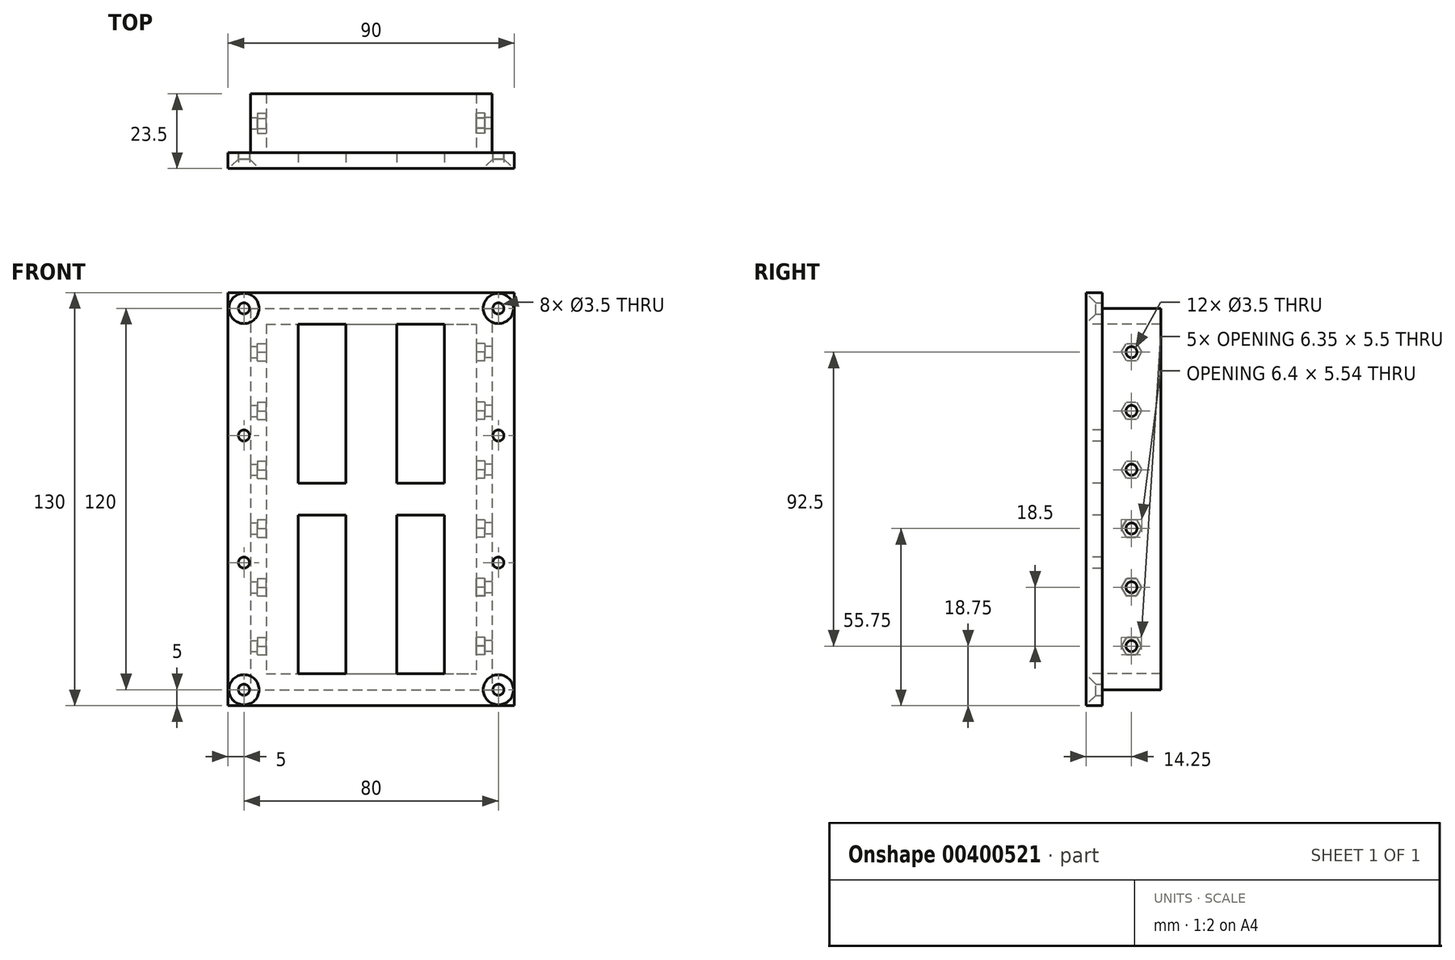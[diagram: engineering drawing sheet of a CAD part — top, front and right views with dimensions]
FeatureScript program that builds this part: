
annotation { "Feature Type Name" : "Feature", "Feature Type Description" : "" }
export const myFeature = defineFeature(function(context is Context, id is Id, definition is map)
    precondition{}
    {
        {
            var Q0;
            Q0=qCreatedBy(makeId("Front.planeOp"),FACE);
            var sketch = newSketch(context, id + "F0", { "sketchPlane" : qUnion([Q0])});
            skLineSegment(sketch, "E0.bottom", {"start": v(-33, 55) * mm, "end": v(33, 55) * mm});
            skLineSegment(sketch, "E0.top", {"start": v(-33, -55) * mm, "end": v(33, -55) * mm});
            skLineSegment(sketch, "E0.left", {"start": v(-33, 55) * mm, "end": v(-33, -55) * mm});
            skLineSegment(sketch, "E0.right", {"start": v(33, 55) * mm, "end": v(33, -55) * mm});
            skPoint(sketch, "E0.middle", {"position": v(0, 0) * mm});
            skLineSegment(sketch, "E1.bottom", {"start": v(-38, 60) * mm, "end": v(38, 60) * mm});
            skLineSegment(sketch, "E1.top", {"start": v(-38, -60) * mm, "end": v(38, -60) * mm});
            skLineSegment(sketch, "E1.left", {"start": v(-38, 60) * mm, "end": v(-38, -60) * mm});
            skLineSegment(sketch, "E1.right", {"start": v(38, 60) * mm, "end": v(38, -60) * mm});
            skSolve(sketch);
        }
        {
            var Q0;
            Q0 = qSketchRegion(id + "F0", true);
            extrude(context, id + "F1", {"entities" : qUnion([Q0]), "oppositeDirection" : true, "depth" : 18.5 * mm});
        }
        {
            var Q0;
            Q0=makeQuery(id+"F1.opExtrude","CAP_FACE",FACE,{"disambiguationData":[OSD([sQuery(id+"F0.wireOp",EDGE,"E0.bottom"),sQuery(id+"F0.wireOp",EDGE,"E0.top"),sQuery(id+"F0.wireOp",EDGE,"E0.left"),sQuery(id+"F0.wireOp",EDGE,"E0.right"),sQuery(id+"F0.wireOp",EDGE,"E1.bottom"),sQuery(id+"F0.wireOp",EDGE,"E1.top"),sQuery(id+"F0.wireOp",EDGE,"E1.left"),sQuery(id+"F0.wireOp",EDGE,"E1.right")])],"isStart":true});
            var sketch = newSketch(context, id + "F2", { "sketchPlane" : qUnion([Q0])});
            skLineSegment(sketch, "E2.bottom", {"start": v(-45, 65) * mm, "end": v(45, 65) * mm});
            skLineSegment(sketch, "E2.top", {"start": v(-45, -65) * mm, "end": v(45, -65) * mm});
            skLineSegment(sketch, "E2.left", {"start": v(-45, 65) * mm, "end": v(-45, -65) * mm});
            skLineSegment(sketch, "E2.right", {"start": v(45, 65) * mm, "end": v(45, -65) * mm});
            skPoint(sketch, "E2.middle", {"position": v(0, 0) * mm});
            skCircle(sketch, "E3", {"center": v(-40, 60) * mm, "radius": 1.75 * mm});
            skCircle(sketch, "E4", {"center": v(40, 60) * mm, "radius": 1.75 * mm});
            skCircle(sketch, "E5", {"center": v(40, -60) * mm, "radius": 1.75 * mm});
            skCircle(sketch, "E6", {"center": v(-40, -60) * mm, "radius": 1.75 * mm});
            skSolve(sketch);
        }
        {
            var Q0;
            Q0=makeQuery(id+"F2.imprint","IMPRINT",FACE,{"disambiguationData":[TD([[makeQuery(id+"F2.imprint","IMPRINT",EDGE,{"derivedFrom":sQuery(id+"F2.wireOp",EDGE,"E2.bottom")}),-1.0]])]});
            var Q1;
            Q1=makeQuery(id+"F2.imprint","IMPRINT",FACE,{"disambiguationData":[TD([[makeQuery(id+"F2.imprint","IMPRINT",EDGE,{"derivedFrom":makeQuery(id+"F1.opExtrude","CAP_EDGE",EDGE,{"disambiguationData":[OSD([sQuery(id+"F0.wireOp",EDGE,"E0.bottom")])],"isStart":true})}),1.0]])]});
            extrude(context, id + "F3", {"entities" : qUnion([Q0, Q1]), "operationType" : NewBodyOperationType.ADD, "depth" : 5 * mm});
        }
        {
            var Q0;
            Q0=makeQuery(id+"F3.opExtrude","CAP_FACE",FACE,{"disambiguationData":[OSD([sQuery(id+"F0.wireOp",EDGE,"E0.bottom"),sQuery(id+"F0.wireOp",EDGE,"E0.top"),sQuery(id+"F0.wireOp",EDGE,"E0.left"),sQuery(id+"F0.wireOp",EDGE,"E0.right"),sQuery(id+"F2.wireOp",EDGE,"E2.bottom"),sQuery(id+"F2.wireOp",EDGE,"E2.top"),sQuery(id+"F2.wireOp",EDGE,"E2.left"),sQuery(id+"F2.wireOp",EDGE,"E2.right"),sQuery(id+"F2.wireOp",EDGE,"E3"),sQuery(id+"F2.wireOp",EDGE,"E4"),sQuery(id+"F2.wireOp",EDGE,"E5"),sQuery(id+"F2.wireOp",EDGE,"E6")])],"isStart":false});
            var sketch = newSketch(context, id + "F4", { "sketchPlane" : qUnion([Q0])});
            skLineSegment(sketch, "E7.bottom", {"start": v(-33, 55) * mm, "end": v(-23, 55) * mm});
            skLineSegment(sketch, "E7.top", {"start": v(-33, -55) * mm, "end": v(-23, -55) * mm});
            skLineSegment(sketch, "E7.left", {"start": v(-33, 55) * mm, "end": v(-33, -55) * mm});
            skLineSegment(sketch, "E7.right", {"start": v(-23, 55) * mm, "end": v(-23, 5) * mm});
            skLineSegment(sketch, "E8.bottom", {"start": v(33, 55) * mm, "end": v(23, 55) * mm});
            skLineSegment(sketch, "E8.top", {"start": v(33, -55) * mm, "end": v(23, -55) * mm});
            skLineSegment(sketch, "E8.left", {"start": v(33, 55) * mm, "end": v(33, -55) * mm});
            skLineSegment(sketch, "E8.right", {"start": v(23, 55) * mm, "end": v(23, 5) * mm});
            skLineSegment(sketch, "E9.bottom", {"start": v(-8, 55) * mm, "end": v(8, 55) * mm});
            skLineSegment(sketch, "E9.top", {"start": v(-8, -55) * mm, "end": v(8, -55) * mm});
            skLineSegment(sketch, "E9.left", {"start": v(-8, 55) * mm, "end": v(-8, 5) * mm});
            skLineSegment(sketch, "E9.right", {"start": v(8, 55) * mm, "end": v(8, 5) * mm});
            skLineSegment(sketch, "E10.bottom", {"start": v(-23, 5) * mm, "end": v(-8, 5) * mm});
            skLineSegment(sketch, "E10.top", {"start": v(-23, -5) * mm, "end": v(-8, -5) * mm});
            skLineSegment(sketch, "E10.left", {"start": v(-33, 5) * mm, "end": v(-33, -5) * mm});
            skLineSegment(sketch, "E10.right", {"start": v(33, 5) * mm, "end": v(33, -5) * mm});
            skPoint(sketch, "E10.middle", {"position": v(0, 0) * mm});
            skLineSegment(sketch, "E11.trimOffspring", {"start": v(-23, -5) * mm, "end": v(-23, -55) * mm});
            skLineSegment(sketch, "E12.trimOffspring", {"start": v(-8, -5) * mm, "end": v(-8, -55) * mm});
            skLineSegment(sketch, "E13.trimOffspring", {"start": v(8, 5) * mm, "end": v(23, 5) * mm});
            skLineSegment(sketch, "E14.trimOffspring", {"start": v(8, -5) * mm, "end": v(23, -5) * mm});
            skLineSegment(sketch, "E15.trimOffspring", {"start": v(8, -5) * mm, "end": v(8, -55) * mm});
            skLineSegment(sketch, "E16.trimOffspring", {"start": v(23, -5) * mm, "end": v(23, -55) * mm});
            skSolve(sketch);
        }
        {
            var Q0;
            {var subQ4=sQuery(id+"F4.wireOp",EDGE,"E7.bottom");Q0=makeQuery(id+"F4.imprint","IMPRINT",FACE,{"disambiguationData":[TD([[makeQuery(id+"F4.imprint","IMPRINT",EDGE,{"derivedFrom":subQ4}),-1.0]])]});}
            extrude(context, id + "F5", {"entities" : qUnion([Q0]), "oppositeDirection" : true, "depth" : 5 * mm});
        }
        {
            var Q0;
            Q0=makeQuery(id+"F5.opExtrude","SWEPT_BODY",BODY,{"disambiguationData":[OSD([sQuery(id+"F4.wireOp",EDGE,"E7.bottom"),sQuery(id+"F4.wireOp",EDGE,"E7.top"),sQuery(id+"F4.wireOp",EDGE,"E7.left"),sQuery(id+"F4.wireOp",EDGE,"E7.right"),sQuery(id+"F4.wireOp",EDGE,"E8.bottom"),sQuery(id+"F4.wireOp",EDGE,"E8.top"),sQuery(id+"F4.wireOp",EDGE,"E8.left"),sQuery(id+"F4.wireOp",EDGE,"E8.right"),sQuery(id+"F4.wireOp",EDGE,"E9.bottom"),sQuery(id+"F4.wireOp",EDGE,"E9.top"),sQuery(id+"F4.wireOp",EDGE,"E9.left"),sQuery(id+"F4.wireOp",EDGE,"E9.right"),sQuery(id+"F4.wireOp",EDGE,"E10.bottom"),sQuery(id+"F4.wireOp",EDGE,"E10.top"),sQuery(id+"F4.wireOp",EDGE,"E10.left"),sQuery(id+"F4.wireOp",EDGE,"E10.right"),sQuery(id+"F4.wireOp",EDGE,"E11.trimOffspring"),sQuery(id+"F4.wireOp",EDGE,"E12.trimOffspring"),sQuery(id+"F4.wireOp",EDGE,"E13.trimOffspring"),sQuery(id+"F4.wireOp",EDGE,"E14.trimOffspring"),sQuery(id+"F4.wireOp",EDGE,"E15.trimOffspring"),sQuery(id+"F4.wireOp",EDGE,"E16.trimOffspring")])]});
            var Q1;
            Q1=makeQuery(id+"F1.opExtrude","SWEPT_BODY",BODY,{"disambiguationData":[OSD([sQuery(id+"F0.wireOp",EDGE,"E0.bottom"),sQuery(id+"F0.wireOp",EDGE,"E0.top"),sQuery(id+"F0.wireOp",EDGE,"E0.left"),sQuery(id+"F0.wireOp",EDGE,"E0.right"),sQuery(id+"F0.wireOp",EDGE,"E1.bottom"),sQuery(id+"F0.wireOp",EDGE,"E1.top"),sQuery(id+"F0.wireOp",EDGE,"E1.left"),sQuery(id+"F0.wireOp",EDGE,"E1.right")])]});
            booleanBodies(context, id + "F6", {"operationType" : BooleanOperationType.UNION, "tools" : qUnion([Q0, Q1])});
        }
        {
            var Q0;
            Q0=makeQuery(id+"F6.opBoolean","MERGE",FACE,{"derivedFrom":[makeQuery(id+"F3.opExtrude","CAP_FACE",FACE,{"disambiguationData":[OSD([sQuery(id+"F0.wireOp",EDGE,"E0.bottom"),sQuery(id+"F0.wireOp",EDGE,"E0.top"),sQuery(id+"F0.wireOp",EDGE,"E0.left"),sQuery(id+"F0.wireOp",EDGE,"E0.right"),sQuery(id+"F2.wireOp",EDGE,"E2.bottom"),sQuery(id+"F2.wireOp",EDGE,"E2.top"),sQuery(id+"F2.wireOp",EDGE,"E2.left"),sQuery(id+"F2.wireOp",EDGE,"E2.right"),sQuery(id+"F2.wireOp",EDGE,"E3"),sQuery(id+"F2.wireOp",EDGE,"E4"),sQuery(id+"F2.wireOp",EDGE,"E5"),sQuery(id+"F2.wireOp",EDGE,"E6")])],"isStart":false}),makeQuery(id+"F5.opExtrude","CAP_FACE",FACE,{"disambiguationData":[OSD([sQuery(id+"F4.wireOp",EDGE,"E7.bottom"),sQuery(id+"F4.wireOp",EDGE,"E7.top"),sQuery(id+"F4.wireOp",EDGE,"E7.left"),sQuery(id+"F4.wireOp",EDGE,"E7.right"),sQuery(id+"F4.wireOp",EDGE,"E8.bottom"),sQuery(id+"F4.wireOp",EDGE,"E8.top"),sQuery(id+"F4.wireOp",EDGE,"E8.left"),sQuery(id+"F4.wireOp",EDGE,"E8.right"),sQuery(id+"F4.wireOp",EDGE,"E9.bottom"),sQuery(id+"F4.wireOp",EDGE,"E9.top"),sQuery(id+"F4.wireOp",EDGE,"E9.left"),sQuery(id+"F4.wireOp",EDGE,"E9.right"),sQuery(id+"F4.wireOp",EDGE,"E10.bottom"),sQuery(id+"F4.wireOp",EDGE,"E10.top"),sQuery(id+"F4.wireOp",EDGE,"E10.left"),sQuery(id+"F4.wireOp",EDGE,"E10.right"),sQuery(id+"F4.wireOp",EDGE,"E11.trimOffspring"),sQuery(id+"F4.wireOp",EDGE,"E12.trimOffspring"),sQuery(id+"F4.wireOp",EDGE,"E13.trimOffspring"),sQuery(id+"F4.wireOp",EDGE,"E14.trimOffspring"),sQuery(id+"F4.wireOp",EDGE,"E15.trimOffspring"),sQuery(id+"F4.wireOp",EDGE,"E16.trimOffspring")])],"isStart":true})]});
            var sketch = newSketch(context, id + "F7", { "sketchPlane" : qUnion([Q0])});
            skCircle(sketch, "E17", {"center": v(-40, 20) * mm, "radius": 1.75 * mm});
            skCircle(sketch, "E18", {"center": v(-40, -20) * mm, "radius": 1.75 * mm});
            skCircle(sketch, "E19", {"center": v(40, -20) * mm, "radius": 1.75 * mm});
            skCircle(sketch, "E20", {"center": v(40, 20) * mm, "radius": 1.75 * mm});
            skSolve(sketch);
        }
        {
            var Q0;
            Q0=makeQuery(id+"F7.imprint","IMPRINT",FACE,{"disambiguationData":[TD([[makeQuery(id+"F7.imprint","IMPRINT",EDGE,{"derivedFrom":sQuery(id+"F7.wireOp",EDGE,"E17")}),1.0]])]});
            var Q1;
            Q1=makeQuery(id+"F7.imprint","IMPRINT",FACE,{"disambiguationData":[TD([[makeQuery(id+"F7.imprint","IMPRINT",EDGE,{"derivedFrom":sQuery(id+"F7.wireOp",EDGE,"E18")}),1.0]])]});
            var Q2;
            Q2=makeQuery(id+"F7.imprint","IMPRINT",FACE,{"disambiguationData":[TD([[makeQuery(id+"F7.imprint","IMPRINT",EDGE,{"derivedFrom":sQuery(id+"F7.wireOp",EDGE,"E19")}),1.0]])]});
            var Q3;
            Q3=makeQuery(id+"F7.imprint","IMPRINT",FACE,{"disambiguationData":[TD([[makeQuery(id+"F7.imprint","IMPRINT",EDGE,{"derivedFrom":sQuery(id+"F7.wireOp",EDGE,"E20")}),1.0]])]});
            extrude(context, id + "F8", {"entities" : qUnion([Q0, Q1, Q2, Q3]), "operationType" : NewBodyOperationType.REMOVE, "oppositeDirection" : true, "depth" : 5 * mm});
        }
        {
            var Q0;
            {var subQ0=sQuery(id+"F0.wireOp",EDGE,"E0.right");Q0=makeQuery(id+"F3.boolean.opBoolean","MERGE",FACE,{"derivedFrom":[makeQuery(id+"F1.opExtrude","SWEPT_FACE",FACE,{"disambiguationData":[OSD([subQ0])]}),makeQuery(id+"F3.opExtrude","SWEPT_FACE",FACE,{"disambiguationData":[OSD([subQ0])]})]});}
            var sketch = newSketch(context, id + "F9", { "sketchPlane" : qUnion([Q0])});
            skLineSegment(sketch, "E21", {"start": v(-9.25, -55) * mm, "end": v(-9.25, 55) * mm});
            skCircle(sketch, "E22", {"center": v(-9.25, -46.25) * mm, "radius": 1.75 * mm});
            skCircle(sketch, "E23", {"center": v(-9.25, -27.75) * mm, "radius": 1.75 * mm});
            skCircle(sketch, "E24", {"center": v(-9.25, -9.25) * mm, "radius": 1.75 * mm});
            skCircle(sketch, "E25", {"center": v(-9.25, 9.25) * mm, "radius": 1.75 * mm});
            skCircle(sketch, "E26", {"center": v(-9.25, 27.75) * mm, "radius": 1.75 * mm});
            skCircle(sketch, "E27", {"center": v(-9.25, 46.25) * mm, "radius": 1.75 * mm});
            skCircle(sketch, "E28.cCircle", {"center": v(-9.25, -46.25) * mm, "radius": 2.75 * mm, "construction": true});
            skLineSegment(sketch, "E28.0", {"start": v(-10.8, -49.02) * mm, "end": v(-12.43, -46.3) * mm});
            skLineSegment(sketch, "E28.1", {"start": v(-12.43, -46.3) * mm, "end": v(-10.87, -43.52) * mm});
            skLineSegment(sketch, "E28.2", {"start": v(-10.87, -43.52) * mm, "end": v(-7.7, -43.48) * mm});
            skLineSegment(sketch, "E28.3", {"start": v(-7.7, -43.48) * mm, "end": v(-6.07, -46.2) * mm});
            skLineSegment(sketch, "E28.4", {"start": v(-6.07, -46.2) * mm, "end": v(-7.63, -48.98) * mm});
            skLineSegment(sketch, "E28.5", {"start": v(-7.63, -48.98) * mm, "end": v(-10.8, -49.02) * mm});
            skPoint(sketch, "E28.0.midPoint", {"position": v(-11.61, -47.66) * mm});
            skCircle(sketch, "E29.cCircle", {"center": v(-9.25, -27.75) * mm, "radius": 2.75 * mm, "construction": true});
            skLineSegment(sketch, "E29.0", {"start": v(-10.8, -30.52) * mm, "end": v(-12.43, -27.8) * mm});
            skLineSegment(sketch, "E29.1", {"start": v(-12.43, -27.8) * mm, "end": v(-10.87, -25.02) * mm});
            skLineSegment(sketch, "E29.2", {"start": v(-10.87, -25.02) * mm, "end": v(-7.7, -24.98) * mm});
            skLineSegment(sketch, "E29.3", {"start": v(-7.7, -24.98) * mm, "end": v(-6.07, -27.7) * mm});
            skLineSegment(sketch, "E29.4", {"start": v(-6.07, -27.7) * mm, "end": v(-7.63, -30.48) * mm});
            skLineSegment(sketch, "E29.5", {"start": v(-7.63, -30.48) * mm, "end": v(-10.8, -30.52) * mm});
            skPoint(sketch, "E29.0.midPoint", {"position": v(-11.61, -29.16) * mm});
            skCircle(sketch, "E30.cCircle", {"center": v(-9.25, -9.25) * mm, "radius": 2.75 * mm, "construction": true});
            skLineSegment(sketch, "E30.0", {"start": v(-7.66, -12) * mm, "end": v(-10.84, -12) * mm});
            skLineSegment(sketch, "E30.1", {"start": v(-10.84, -12) * mm, "end": v(-12.43, -9.25) * mm});
            skLineSegment(sketch, "E30.2", {"start": v(-12.43, -9.25) * mm, "end": v(-10.84, -6.5) * mm});
            skLineSegment(sketch, "E30.3", {"start": v(-10.84, -6.5) * mm, "end": v(-7.66, -6.5) * mm});
            skLineSegment(sketch, "E30.4", {"start": v(-7.66, -6.5) * mm, "end": v(-6.07, -9.25) * mm});
            skLineSegment(sketch, "E30.5", {"start": v(-6.07, -9.25) * mm, "end": v(-7.66, -12) * mm});
            skPoint(sketch, "E30.0.midPoint", {"position": v(-9.25, -12) * mm});
            skCircle(sketch, "E31.cCircle", {"center": v(-9.25, 9.25) * mm, "radius": 2.75 * mm, "construction": true});
            skLineSegment(sketch, "E31.0", {"start": v(-7.66, 6.5) * mm, "end": v(-10.84, 6.5) * mm});
            skLineSegment(sketch, "E31.1", {"start": v(-10.84, 6.5) * mm, "end": v(-12.43, 9.25) * mm});
            skLineSegment(sketch, "E31.2", {"start": v(-12.43, 9.25) * mm, "end": v(-10.84, 12) * mm});
            skLineSegment(sketch, "E31.3", {"start": v(-10.84, 12) * mm, "end": v(-7.66, 12) * mm});
            skLineSegment(sketch, "E31.4", {"start": v(-7.66, 12) * mm, "end": v(-6.07, 9.25) * mm});
            skLineSegment(sketch, "E31.5", {"start": v(-6.07, 9.25) * mm, "end": v(-7.66, 6.5) * mm});
            skPoint(sketch, "E31.0.midPoint", {"position": v(-9.25, 6.5) * mm});
            skCircle(sketch, "E32.cCircle", {"center": v(-9.25, 27.75) * mm, "radius": 2.75 * mm, "construction": true});
            skLineSegment(sketch, "E32.0", {"start": v(-7.66, 25) * mm, "end": v(-10.84, 25) * mm});
            skLineSegment(sketch, "E32.1", {"start": v(-10.84, 25) * mm, "end": v(-12.43, 27.75) * mm});
            skLineSegment(sketch, "E32.2", {"start": v(-12.43, 27.75) * mm, "end": v(-10.84, 30.5) * mm});
            skLineSegment(sketch, "E32.3", {"start": v(-10.84, 30.5) * mm, "end": v(-7.66, 30.5) * mm});
            skLineSegment(sketch, "E32.4", {"start": v(-7.66, 30.5) * mm, "end": v(-6.07, 27.75) * mm});
            skLineSegment(sketch, "E32.5", {"start": v(-6.07, 27.75) * mm, "end": v(-7.66, 25) * mm});
            skPoint(sketch, "E32.0.midPoint", {"position": v(-9.25, 25) * mm});
            skCircle(sketch, "E33.cCircle", {"center": v(-9.25, 46.25) * mm, "radius": 2.75 * mm, "construction": true});
            skLineSegment(sketch, "E33.0", {"start": v(-7.66, 43.5) * mm, "end": v(-10.84, 43.5) * mm});
            skLineSegment(sketch, "E33.1", {"start": v(-10.84, 43.5) * mm, "end": v(-12.43, 46.25) * mm});
            skLineSegment(sketch, "E33.2", {"start": v(-12.43, 46.25) * mm, "end": v(-10.84, 49) * mm});
            skLineSegment(sketch, "E33.3", {"start": v(-10.84, 49) * mm, "end": v(-7.66, 49) * mm});
            skLineSegment(sketch, "E33.4", {"start": v(-7.66, 49) * mm, "end": v(-6.07, 46.25) * mm});
            skLineSegment(sketch, "E33.5", {"start": v(-6.07, 46.25) * mm, "end": v(-7.66, 43.5) * mm});
            skPoint(sketch, "E33.0.midPoint", {"position": v(-9.25, 43.5) * mm});
            skSolve(sketch);
        }
        {
            var Q0;
            Q0 = qSketchRegion(id + "F9", true);
            extrude(context, id + "F10", {"entities" : qUnion([Q0]), "operationType" : NewBodyOperationType.REMOVE, "oppositeDirection" : true, "depth" : 2.75 * mm});
        }
        {
            var Q0;
            {var subQ0=sQuery(id+"F0.wireOp",EDGE,"E0.right");Q0=makeQuery(id+"F10.boolean.opBoolean","SPLIT",FACE,{"disambiguationData":[TD([makeQuery(id+"F10.opExtrude","SWEPT_FACE",FACE,{"disambiguationData":[OSD([sQuery(id+"F9.wireOp",EDGE,"E22")])]})])],"derivedFrom":makeQuery(id+"F3.boolean.opBoolean","MERGE",FACE,{"derivedFrom":[makeQuery(id+"F1.opExtrude","SWEPT_FACE",FACE,{"disambiguationData":[OSD([subQ0])]}),makeQuery(id+"F3.opExtrude","SWEPT_FACE",FACE,{"disambiguationData":[OSD([subQ0])]})]})});}
            var Q1;
            {var subQ0=sQuery(id+"F0.wireOp",EDGE,"E0.right");Q1=makeQuery(id+"F10.boolean.opBoolean","SPLIT",FACE,{"disambiguationData":[TD([makeQuery(id+"F10.opExtrude","SWEPT_FACE",FACE,{"disambiguationData":[OSD([sQuery(id+"F9.wireOp",EDGE,"E23")])]})])],"derivedFrom":makeQuery(id+"F3.boolean.opBoolean","MERGE",FACE,{"derivedFrom":[makeQuery(id+"F1.opExtrude","SWEPT_FACE",FACE,{"disambiguationData":[OSD([subQ0])]}),makeQuery(id+"F3.opExtrude","SWEPT_FACE",FACE,{"disambiguationData":[OSD([subQ0])]})]})});}
            var Q2;
            {var subQ0=sQuery(id+"F0.wireOp",EDGE,"E0.right");Q2=makeQuery(id+"F10.boolean.opBoolean","SPLIT",FACE,{"disambiguationData":[TD([makeQuery(id+"F10.opExtrude","SWEPT_FACE",FACE,{"disambiguationData":[OSD([sQuery(id+"F9.wireOp",EDGE,"E24")])]})])],"derivedFrom":makeQuery(id+"F3.boolean.opBoolean","MERGE",FACE,{"derivedFrom":[makeQuery(id+"F1.opExtrude","SWEPT_FACE",FACE,{"disambiguationData":[OSD([subQ0])]}),makeQuery(id+"F3.opExtrude","SWEPT_FACE",FACE,{"disambiguationData":[OSD([subQ0])]})]})});}
            var Q3;
            {var subQ0=sQuery(id+"F0.wireOp",EDGE,"E0.right");Q3=makeQuery(id+"F10.boolean.opBoolean","SPLIT",FACE,{"disambiguationData":[TD([makeQuery(id+"F10.opExtrude","SWEPT_FACE",FACE,{"disambiguationData":[OSD([sQuery(id+"F9.wireOp",EDGE,"E25")])]})])],"derivedFrom":makeQuery(id+"F3.boolean.opBoolean","MERGE",FACE,{"derivedFrom":[makeQuery(id+"F1.opExtrude","SWEPT_FACE",FACE,{"disambiguationData":[OSD([subQ0])]}),makeQuery(id+"F3.opExtrude","SWEPT_FACE",FACE,{"disambiguationData":[OSD([subQ0])]})]})});}
            var Q4;
            {var subQ0=sQuery(id+"F0.wireOp",EDGE,"E0.right");Q4=makeQuery(id+"F10.boolean.opBoolean","SPLIT",FACE,{"disambiguationData":[TD([makeQuery(id+"F10.opExtrude","SWEPT_FACE",FACE,{"disambiguationData":[OSD([sQuery(id+"F9.wireOp",EDGE,"E26")])]})])],"derivedFrom":makeQuery(id+"F3.boolean.opBoolean","MERGE",FACE,{"derivedFrom":[makeQuery(id+"F1.opExtrude","SWEPT_FACE",FACE,{"disambiguationData":[OSD([subQ0])]}),makeQuery(id+"F3.opExtrude","SWEPT_FACE",FACE,{"disambiguationData":[OSD([subQ0])]})]})});}
            var Q5;
            {var subQ0=sQuery(id+"F0.wireOp",EDGE,"E0.right");Q5=makeQuery(id+"F10.boolean.opBoolean","SPLIT",FACE,{"disambiguationData":[TD([makeQuery(id+"F10.opExtrude","SWEPT_FACE",FACE,{"disambiguationData":[OSD([sQuery(id+"F9.wireOp",EDGE,"E27")])]})])],"derivedFrom":makeQuery(id+"F3.boolean.opBoolean","MERGE",FACE,{"derivedFrom":[makeQuery(id+"F1.opExtrude","SWEPT_FACE",FACE,{"disambiguationData":[OSD([subQ0])]}),makeQuery(id+"F3.opExtrude","SWEPT_FACE",FACE,{"disambiguationData":[OSD([subQ0])]})]})});}
            extrude(context, id + "F11", {"entities" : qUnion([Q0, Q1, Q2, Q3, Q4, Q5]), "operationType" : NewBodyOperationType.REMOVE, "oppositeDirection" : true, "depth" : 10 * mm});
        }
        {
            var Q0;
            Q0=makeQuery(id+"F3.opExtrude","CAP_EDGE",EDGE,{"disambiguationData":[OSD([sQuery(id+"F2.wireOp",EDGE,"E5")])],"isStart":false});
            var Q1;
            Q1=makeQuery(id+"F8.boolean.opBoolean","COPY",EDGE,{"derivedFrom":makeQuery(id+"F8.opExtrude","CAP_EDGE",EDGE,{"disambiguationData":[OSD([sQuery(id+"F7.wireOp",EDGE,"E19")])],"isStart":true})});
            var Q2;
            Q2=makeQuery(id+"F8.boolean.opBoolean","COPY",EDGE,{"derivedFrom":makeQuery(id+"F8.opExtrude","CAP_EDGE",EDGE,{"disambiguationData":[OSD([sQuery(id+"F7.wireOp",EDGE,"E20")])],"isStart":true})});
            var Q3;
            Q3=makeQuery(id+"F3.opExtrude","CAP_EDGE",EDGE,{"disambiguationData":[OSD([sQuery(id+"F2.wireOp",EDGE,"E4")])],"isStart":false});
            var Q4;
            Q4=makeQuery(id+"F3.opExtrude","CAP_EDGE",EDGE,{"disambiguationData":[OSD([sQuery(id+"F2.wireOp",EDGE,"E3")])],"isStart":false});
            var Q5;
            Q5=makeQuery(id+"F8.boolean.opBoolean","COPY",EDGE,{"derivedFrom":makeQuery(id+"F8.opExtrude","CAP_EDGE",EDGE,{"disambiguationData":[OSD([sQuery(id+"F7.wireOp",EDGE,"E17")])],"isStart":true})});
            var Q6;
            Q6=makeQuery(id+"F8.boolean.opBoolean","COPY",EDGE,{"derivedFrom":makeQuery(id+"F8.opExtrude","CAP_EDGE",EDGE,{"disambiguationData":[OSD([sQuery(id+"F7.wireOp",EDGE,"E18")])],"isStart":true})});
            var Q7;
            Q7=makeQuery(id+"F3.opExtrude","CAP_EDGE",EDGE,{"disambiguationData":[OSD([sQuery(id+"F2.wireOp",EDGE,"E6")])],"isStart":false});
            chamfer(context, id + "F12", {"entities" : qUnion([Q0, Q1, Q2, Q3, Q4, Q5, Q6, Q7]), "width" : 3 * mm, "tangentPropagation" : true});
        }
        {
            var Q0;
            {var subQ0=sQuery(id+"F0.wireOp",EDGE,"E0.left");Q0=makeQuery(id+"F3.boolean.opBoolean","MERGE",FACE,{"derivedFrom":[makeQuery(id+"F1.opExtrude","SWEPT_FACE",FACE,{"disambiguationData":[OSD([subQ0])]}),makeQuery(id+"F3.opExtrude","SWEPT_FACE",FACE,{"disambiguationData":[OSD([subQ0])]})]});}
            var sketch = newSketch(context, id + "F13", { "sketchPlane" : qUnion([Q0])});
            skLineSegment(sketch, "E34", {"start": v(9.25, 55) * mm, "end": v(9.25, -55) * mm});
            skCircle(sketch, "E35", {"center": v(9.25, 46.25) * mm, "radius": 1.75 * mm});
            skCircle(sketch, "E36", {"center": v(9.25, 27.75) * mm, "radius": 1.75 * mm});
            skCircle(sketch, "E37", {"center": v(9.25, 9.25) * mm, "radius": 1.75 * mm});
            skCircle(sketch, "E38", {"center": v(9.25, -9.25) * mm, "radius": 1.75 * mm});
            skCircle(sketch, "E39", {"center": v(9.25, -27.75) * mm, "radius": 1.75 * mm});
            skCircle(sketch, "E40", {"center": v(9.25, -46.25) * mm, "radius": 1.75 * mm});
            skCircle(sketch, "E41.cCircle", {"center": v(9.25, 46.25) * mm, "radius": 2.75 * mm, "construction": true});
            skLineSegment(sketch, "E41.0", {"start": v(7.66, 49) * mm, "end": v(10.84, 49) * mm});
            skLineSegment(sketch, "E41.1", {"start": v(10.84, 49) * mm, "end": v(12.43, 46.25) * mm});
            skLineSegment(sketch, "E41.2", {"start": v(12.43, 46.25) * mm, "end": v(10.84, 43.5) * mm});
            skLineSegment(sketch, "E41.3", {"start": v(10.84, 43.5) * mm, "end": v(7.66, 43.5) * mm});
            skLineSegment(sketch, "E41.4", {"start": v(7.66, 43.5) * mm, "end": v(6.07, 46.25) * mm});
            skLineSegment(sketch, "E41.5", {"start": v(6.07, 46.25) * mm, "end": v(7.66, 49) * mm});
            skPoint(sketch, "E41.0.midPoint", {"position": v(9.25, 49) * mm});
            skCircle(sketch, "E42.cCircle", {"center": v(9.25, 27.75) * mm, "radius": 2.75 * mm, "construction": true});
            skLineSegment(sketch, "E42.0", {"start": v(7.66, 30.5) * mm, "end": v(10.84, 30.5) * mm});
            skLineSegment(sketch, "E42.1", {"start": v(10.84, 30.5) * mm, "end": v(12.43, 27.75) * mm});
            skLineSegment(sketch, "E42.2", {"start": v(12.43, 27.75) * mm, "end": v(10.84, 25) * mm});
            skLineSegment(sketch, "E42.3", {"start": v(10.84, 25) * mm, "end": v(7.66, 25) * mm});
            skLineSegment(sketch, "E42.4", {"start": v(7.66, 25) * mm, "end": v(6.07, 27.75) * mm});
            skLineSegment(sketch, "E42.5", {"start": v(6.07, 27.75) * mm, "end": v(7.66, 30.5) * mm});
            skPoint(sketch, "E42.0.midPoint", {"position": v(9.25, 30.5) * mm});
            skCircle(sketch, "E43.cCircle", {"center": v(9.25, 9.25) * mm, "radius": 2.75 * mm, "construction": true});
            skLineSegment(sketch, "E43.0", {"start": v(7.66, 12) * mm, "end": v(10.84, 12) * mm});
            skLineSegment(sketch, "E43.1", {"start": v(10.84, 12) * mm, "end": v(12.43, 9.25) * mm});
            skLineSegment(sketch, "E43.2", {"start": v(12.43, 9.25) * mm, "end": v(10.84, 6.5) * mm});
            skLineSegment(sketch, "E43.3", {"start": v(10.84, 6.5) * mm, "end": v(7.66, 6.5) * mm});
            skLineSegment(sketch, "E43.4", {"start": v(7.66, 6.5) * mm, "end": v(6.07, 9.25) * mm});
            skLineSegment(sketch, "E43.5", {"start": v(6.07, 9.25) * mm, "end": v(7.66, 12) * mm});
            skPoint(sketch, "E43.0.midPoint", {"position": v(9.25, 12) * mm});
            skCircle(sketch, "E44.cCircle", {"center": v(9.25, -9.25) * mm, "radius": 2.77 * mm, "construction": true});
            skLineSegment(sketch, "E44.0", {"start": v(7.65, -6.48) * mm, "end": v(10.85, -6.48) * mm});
            skLineSegment(sketch, "E44.1", {"start": v(10.85, -6.48) * mm, "end": v(12.45, -9.25) * mm});
            skLineSegment(sketch, "E44.2", {"start": v(12.45, -9.25) * mm, "end": v(10.85, -12.02) * mm});
            skLineSegment(sketch, "E44.3", {"start": v(10.85, -12.02) * mm, "end": v(7.65, -12.02) * mm});
            skLineSegment(sketch, "E44.4", {"start": v(7.65, -12.02) * mm, "end": v(6.05, -9.25) * mm});
            skLineSegment(sketch, "E44.5", {"start": v(6.05, -9.25) * mm, "end": v(7.65, -6.48) * mm});
            skPoint(sketch, "E44.0.midPoint", {"position": v(9.25, -6.48) * mm});
            skCircle(sketch, "E45.cCircle", {"center": v(9.25, -27.75) * mm, "radius": 2.75 * mm, "construction": true});
            skLineSegment(sketch, "E45.0", {"start": v(7.66, -25) * mm, "end": v(10.84, -25) * mm});
            skLineSegment(sketch, "E45.1", {"start": v(10.84, -25) * mm, "end": v(12.43, -27.75) * mm});
            skLineSegment(sketch, "E45.2", {"start": v(12.43, -27.75) * mm, "end": v(10.84, -30.5) * mm});
            skLineSegment(sketch, "E45.3", {"start": v(10.84, -30.5) * mm, "end": v(7.66, -30.5) * mm});
            skLineSegment(sketch, "E45.4", {"start": v(7.66, -30.5) * mm, "end": v(6.07, -27.75) * mm});
            skLineSegment(sketch, "E45.5", {"start": v(6.07, -27.75) * mm, "end": v(7.66, -25) * mm});
            skPoint(sketch, "E45.0.midPoint", {"position": v(9.25, -25) * mm});
            skCircle(sketch, "E46.cCircle", {"center": v(9.25, -46.25) * mm, "radius": 2.75 * mm, "construction": true});
            skLineSegment(sketch, "E46.0", {"start": v(7.66, -43.5) * mm, "end": v(10.84, -43.5) * mm});
            skLineSegment(sketch, "E46.1", {"start": v(10.84, -43.5) * mm, "end": v(12.43, -46.25) * mm});
            skLineSegment(sketch, "E46.2", {"start": v(12.43, -46.25) * mm, "end": v(10.84, -49) * mm});
            skLineSegment(sketch, "E46.3", {"start": v(10.84, -49) * mm, "end": v(7.66, -49) * mm});
            skLineSegment(sketch, "E46.4", {"start": v(7.66, -49) * mm, "end": v(6.07, -46.25) * mm});
            skLineSegment(sketch, "E46.5", {"start": v(6.07, -46.25) * mm, "end": v(7.66, -43.5) * mm});
            skPoint(sketch, "E46.0.midPoint", {"position": v(9.25, -43.5) * mm});
            skSolve(sketch);
        }
        {
            var Q0;
            Q0 = qSketchRegion(id + "F13", true);
            extrude(context, id + "F14", {"entities" : qUnion([Q0]), "operationType" : NewBodyOperationType.REMOVE, "oppositeDirection" : true, "depth" : 2.75 * mm});
        }
        {
            var Q0;
            {var subQ0=sQuery(id+"F0.wireOp",EDGE,"E0.left");Q0=makeQuery(id+"F14.boolean.opBoolean","SPLIT",FACE,{"disambiguationData":[TD([makeQuery(id+"F14.opExtrude","SWEPT_FACE",FACE,{"disambiguationData":[OSD([sQuery(id+"F13.wireOp",EDGE,"E35")])]})])],"derivedFrom":makeQuery(id+"F3.boolean.opBoolean","MERGE",FACE,{"derivedFrom":[makeQuery(id+"F1.opExtrude","SWEPT_FACE",FACE,{"disambiguationData":[OSD([subQ0])]}),makeQuery(id+"F3.opExtrude","SWEPT_FACE",FACE,{"disambiguationData":[OSD([subQ0])]})]})});}
            var Q1;
            {var subQ0=sQuery(id+"F0.wireOp",EDGE,"E0.left");Q1=makeQuery(id+"F14.boolean.opBoolean","SPLIT",FACE,{"disambiguationData":[TD([makeQuery(id+"F14.opExtrude","SWEPT_FACE",FACE,{"disambiguationData":[OSD([sQuery(id+"F13.wireOp",EDGE,"E36")])]})])],"derivedFrom":makeQuery(id+"F3.boolean.opBoolean","MERGE",FACE,{"derivedFrom":[makeQuery(id+"F1.opExtrude","SWEPT_FACE",FACE,{"disambiguationData":[OSD([subQ0])]}),makeQuery(id+"F3.opExtrude","SWEPT_FACE",FACE,{"disambiguationData":[OSD([subQ0])]})]})});}
            var Q2;
            {var subQ0=sQuery(id+"F0.wireOp",EDGE,"E0.left");Q2=makeQuery(id+"F14.boolean.opBoolean","SPLIT",FACE,{"disambiguationData":[TD([makeQuery(id+"F14.opExtrude","SWEPT_FACE",FACE,{"disambiguationData":[OSD([sQuery(id+"F13.wireOp",EDGE,"E37")])]})])],"derivedFrom":makeQuery(id+"F3.boolean.opBoolean","MERGE",FACE,{"derivedFrom":[makeQuery(id+"F1.opExtrude","SWEPT_FACE",FACE,{"disambiguationData":[OSD([subQ0])]}),makeQuery(id+"F3.opExtrude","SWEPT_FACE",FACE,{"disambiguationData":[OSD([subQ0])]})]})});}
            var Q3;
            {var subQ0=sQuery(id+"F0.wireOp",EDGE,"E0.left");Q3=makeQuery(id+"F14.boolean.opBoolean","SPLIT",FACE,{"disambiguationData":[TD([makeQuery(id+"F14.opExtrude","SWEPT_FACE",FACE,{"disambiguationData":[OSD([sQuery(id+"F13.wireOp",EDGE,"E38")])]})])],"derivedFrom":makeQuery(id+"F3.boolean.opBoolean","MERGE",FACE,{"derivedFrom":[makeQuery(id+"F1.opExtrude","SWEPT_FACE",FACE,{"disambiguationData":[OSD([subQ0])]}),makeQuery(id+"F3.opExtrude","SWEPT_FACE",FACE,{"disambiguationData":[OSD([subQ0])]})]})});}
            var Q4;
            {var subQ0=sQuery(id+"F0.wireOp",EDGE,"E0.left");Q4=makeQuery(id+"F14.boolean.opBoolean","SPLIT",FACE,{"disambiguationData":[TD([makeQuery(id+"F14.opExtrude","SWEPT_FACE",FACE,{"disambiguationData":[OSD([sQuery(id+"F13.wireOp",EDGE,"E39")])]})])],"derivedFrom":makeQuery(id+"F3.boolean.opBoolean","MERGE",FACE,{"derivedFrom":[makeQuery(id+"F1.opExtrude","SWEPT_FACE",FACE,{"disambiguationData":[OSD([subQ0])]}),makeQuery(id+"F3.opExtrude","SWEPT_FACE",FACE,{"disambiguationData":[OSD([subQ0])]})]})});}
            var Q5;
            {var subQ0=sQuery(id+"F0.wireOp",EDGE,"E0.left");Q5=makeQuery(id+"F14.boolean.opBoolean","SPLIT",FACE,{"disambiguationData":[TD([makeQuery(id+"F14.opExtrude","SWEPT_FACE",FACE,{"disambiguationData":[OSD([sQuery(id+"F13.wireOp",EDGE,"E40")])]})])],"derivedFrom":makeQuery(id+"F3.boolean.opBoolean","MERGE",FACE,{"derivedFrom":[makeQuery(id+"F1.opExtrude","SWEPT_FACE",FACE,{"disambiguationData":[OSD([subQ0])]}),makeQuery(id+"F3.opExtrude","SWEPT_FACE",FACE,{"disambiguationData":[OSD([subQ0])]})]})});}
            extrude(context, id + "F15", {"entities" : qUnion([Q0, Q1, Q2, Q3, Q4, Q5]), "operationType" : NewBodyOperationType.REMOVE, "oppositeDirection" : true, "depth" : 10 * mm});
        }
    });
